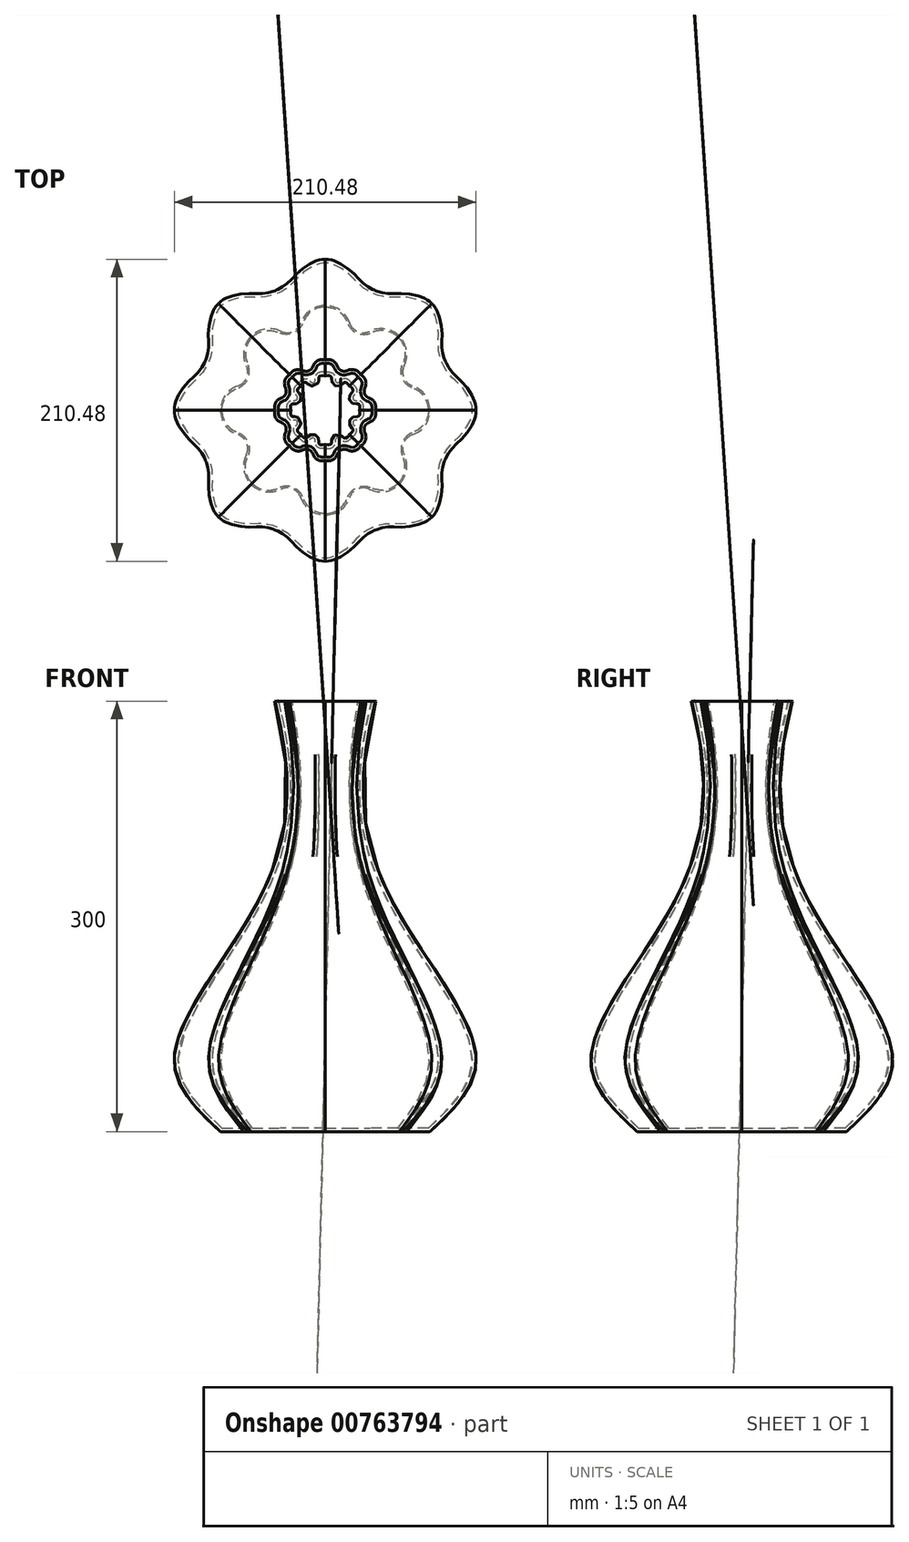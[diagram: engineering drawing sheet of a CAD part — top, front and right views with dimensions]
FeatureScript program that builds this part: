
annotation { "Feature Type Name" : "Feature", "Feature Type Description" : "" }
export const myFeature = defineFeature(function(context is Context, id is Id, definition is map)
    precondition{}
    {
        {
            var Q0;
            Q0=qCreatedBy(makeId("Top.planeOp"),FACE);
            var sketch = newSketch(context, id + "F0", { "sketchPlane" : qUnion([Q0])});
            skCircle(sketch, "E0", {"center": v(0, 0) * mm, "radius": 73 * mm, "construction": true});
            skArc(sketch, "E1", {"start": v(17.04, 60.79) * mm, "mid": v(10.48, 69.63) * mm, "end": v(0, 73) * mm});
            skArc(sketch, "E2", {"start": v(51.62, 51.62) * mm, "mid": v(41.82, 56.65) * mm, "end": v(30.93, 55.04) * mm});
            skArc(sketch, "E3", {"start": v(17.04, 60.79) * mm, "mid": v(22.69, 54.77) * mm, "end": v(30.93, 55.04) * mm});
            skArc(sketch, "E4", {"start": v(8.57, 30.58) * mm, "mid": v(11.4, 27.54) * mm, "end": v(15.56, 27.69) * mm, "construction": true});
            skArc(sketch, "E5", {"start": v(8.57, 30.58) * mm, "mid": v(5.2, 34.55) * mm, "end": v(0, 35.03) * mm, "construction": true});
            skArc(sketch, "E6.MirrorCS", {"start": v(15.56, 27.69) * mm, "mid": v(20.76, 28.1) * mm, "end": v(24.77, 24.77) * mm, "construction": true});
            skLineSegment(sketch, "E7", {"start": v(0, 0) * mm, "end": v(0, 73) * mm});
            skLineSegment(sketch, "E8", {"start": v(0, 0) * mm, "end": v(51.62, 51.62) * mm});
            skSolve(sketch);
        }
        {
            var Q0;
            Q0=qCreatedBy(makeId("Top.planeOp"),FACE);
            cPlane(context, id + "F1", {"entities" : qUnion([Q0]), "cplaneType" : CPlaneType.OFFSET, "offset" : 300 * mm, "width" : 150 * mm, "height" : 150 * mm});
        }
        {
            var Q0;
            Q0=qCreatedBy(id+"F1.planeOp",FACE);
            var sketch = newSketch(context, id + "F2", { "sketchPlane" : qUnion([Q0])});
            skArc(sketch, "E9.0", {"start": v(8.57, 30.58) * mm, "mid": v(5.2, 34.55) * mm, "end": v(0, 35.03) * mm});
            skArc(sketch, "E9.1", {"start": v(8.57, 30.58) * mm, "mid": v(11.4, 27.54) * mm, "end": v(15.56, 27.69) * mm});
            skArc(sketch, "E9.2", {"start": v(15.56, 27.69) * mm, "mid": v(20.76, 28.1) * mm, "end": v(24.77, 24.77) * mm});
            skLineSegment(sketch, "E10.0", {"start": v(0, 0) * mm, "end": v(51.62, 51.62) * mm});
            skLineSegment(sketch, "E10.1", {"start": v(0, 0) * mm, "end": v(0, 73) * mm});
            skSolve(sketch);
        }
        {
            var Q0;
            Q0=qCreatedBy(makeId("Right.planeOp"),FACE);
            var sketch = newSketch(context, id + "F3", { "sketchPlane" : qUnion([Q0])});
            skPoint(sketch, "E11.0", {"position": v(73, 0) * mm});
            skPoint(sketch, "E12.0", {"position": v(35.03, 300) * mm});
            skFitSpline(sketch, "E13", {"points": [v(73, 0) * mm, v(105.18, 51.77) * mm, v(44.21, 165.24) * mm, v(35.03, 300) * mm], "startDerivative": vector(198.77, 183.99) * mm, "endDerivative": vector(106.37, 417) * mm});
            skSolve(sketch);
        }
        {
            var Q0;
            Q0=sQuery(id+"F2.wireOp",VERTEX,"E10.0.start");
            var Q1;
            Q1=sQuery(id+"F2.wireOp",VERTEX,"E10.0.end");
            var Q2;
            Q2=sQuery(id+"F0.wireOp",VERTEX,"E8.end");
            cPlane(context, id + "F4", {"entities" : qUnion([Q0, Q1, Q2]), "cplaneType" : CPlaneType.THREE_POINT, "offset" : 25 * mm, "width" : 150 * mm, "height" : 150 * mm});
        }
        {
            var Q0;
            Q0=qCreatedBy(id+"F4.planeOp",FACE);
            var sketch = newSketch(context, id + "F5", { "sketchPlane" : qUnion([Q0])});
            skPoint(sketch, "E14.0", {"position": v(73, 0) * mm});
            skPoint(sketch, "E15.0", {"position": v(35.03, 300) * mm});
            skFitSpline(sketch, "E16", {"points": [v(73, 0) * mm, v(105.18, 51.77) * mm, v(44.21, 165.24) * mm, v(35.03, 300) * mm], "startDerivative": vector(198.77, 183.99) * mm, "endDerivative": vector(106.37, 417) * mm});
            skSolve(sketch);
        }
        {
            var Q0;
            Q0=makeQuery(id+"F0.imprint","IMPRINT",FACE,{"disambiguationData":[TD([[makeQuery(id+"F0.imprint","IMPRINT",EDGE,{"derivedFrom":sQuery(id+"F0.wireOp",EDGE,"E1")}),1.0]])]});
            var Q1;
            {var subQ4=sQuery(id+"F2.wireOp",EDGE,"E9.0");Q1=makeQuery(id+"F2.imprint","IMPRINT",FACE,{"disambiguationData":[TD([[makeQuery(id+"F2.imprint","IMPRINT",EDGE,{"derivedFrom":subQ4}),1.0]])]});}
            var Q2;
            Q2=sQuery(id+"F5.wireOp",EDGE,"E16");
            var Q3;
            Q3=sQuery(id+"F3.wireOp",EDGE,"E13");
            loft(context, id + "F6", {"addGuides" : true, "sheetProfilesArray" : [{ "sheetProfileEntities" : qUnion([Q0]) }, { "sheetProfileEntities" : qUnion([Q1]) }], "guidesArray" : [{ "guideEntities" : qUnion([Q2]), "guideDerivativeType" : LoftGuideDerivativeType.DEFAULT, "guideDerivativeMagnitude" : 1 }, { "guideEntities" : qUnion([Q3]), "guideDerivativeType" : LoftGuideDerivativeType.DEFAULT, "guideDerivativeMagnitude" : 1 }]});
        }
        {
            var Q0;
            Q0=qCreatedBy(makeId("Right.planeOp"),FACE);
            var sketch = newSketch(context, id + "F7", { "sketchPlane" : qUnion([Q0])});
            skLineSegment(sketch, "E17", {"start": v(0, 302.23) * mm, "end": v(0, 0) * mm});
            skSolve(sketch);
        }
        {
            var Q0;
            {var subQ4=sQuery(id+"F2.wireOp",EDGE,"E9.0");Q0=makeQuery(id+"F6.opLoft","SWEPT_BODY",BODY,{"disambiguationData":[OSD([makeQuery(id+"F0.imprint","IMPRINT",FACE,{"disambiguationData":[TD([[makeQuery(id+"F0.imprint","IMPRINT",EDGE,{"derivedFrom":sQuery(id+"F0.wireOp",EDGE,"E1")}),1.0]])]}),makeQuery(id+"F2.imprint","IMPRINT",FACE,{"disambiguationData":[TD([[makeQuery(id+"F2.imprint","IMPRINT",EDGE,{"derivedFrom":subQ4}),1.0]])]}),sQuery(id+"F3.wireOp",EDGE,"E13"),sQuery(id+"F5.wireOp",EDGE,"E16")])]});}
            var Q1;
            Q1=sQuery(id+"F7.wireOp",EDGE,"E17");
            circularPattern(context, id + "F8", {"operationType" : NewBodyOperationType.ADD, "entities" : qUnion([Q0]), "axis" : qUnion([Q1]), "angle" : 360 * degree, "instanceCount" : 8, "equalSpace" : true});
        }
        {
            var Q0;
            {var subQ4=sQuery(id+"F2.wireOp",EDGE,"E9.0");var subQ5=makeQuery(id+"F6.opLoft","CAP_FACE",FACE,{"disambiguationData":[OSD([makeQuery(id+"F2.imprint","IMPRINT",FACE,{"disambiguationData":[TD([[makeQuery(id+"F2.imprint","IMPRINT",EDGE,{"derivedFrom":subQ4}),1.0]])]})])],"isStart":true});Q0=makeQuery(id+"F8.boolean.opBoolean","MERGE",FACE,{"derivedFrom":[subQ5,makeQuery(id+"F8.opPattern","COPY",FACE,{"derivedFrom":subQ5,"instanceName":"1"}),makeQuery(id+"F8.opPattern","COPY",FACE,{"derivedFrom":subQ5,"instanceName":"2"}),makeQuery(id+"F8.opPattern","COPY",FACE,{"derivedFrom":subQ5,"instanceName":"3"}),makeQuery(id+"F8.opPattern","COPY",FACE,{"derivedFrom":subQ5,"instanceName":"4"}),makeQuery(id+"F8.opPattern","COPY",FACE,{"derivedFrom":subQ5,"instanceName":"5"}),makeQuery(id+"F8.opPattern","COPY",FACE,{"derivedFrom":subQ5,"instanceName":"6"}),makeQuery(id+"F8.opPattern","COPY",FACE,{"derivedFrom":subQ5,"instanceName":"7"})]});}
            shell(context, id + "F9", {"entities" : qUnion([Q0]), "thickness" : 2.5 * mm});
        }
    });
